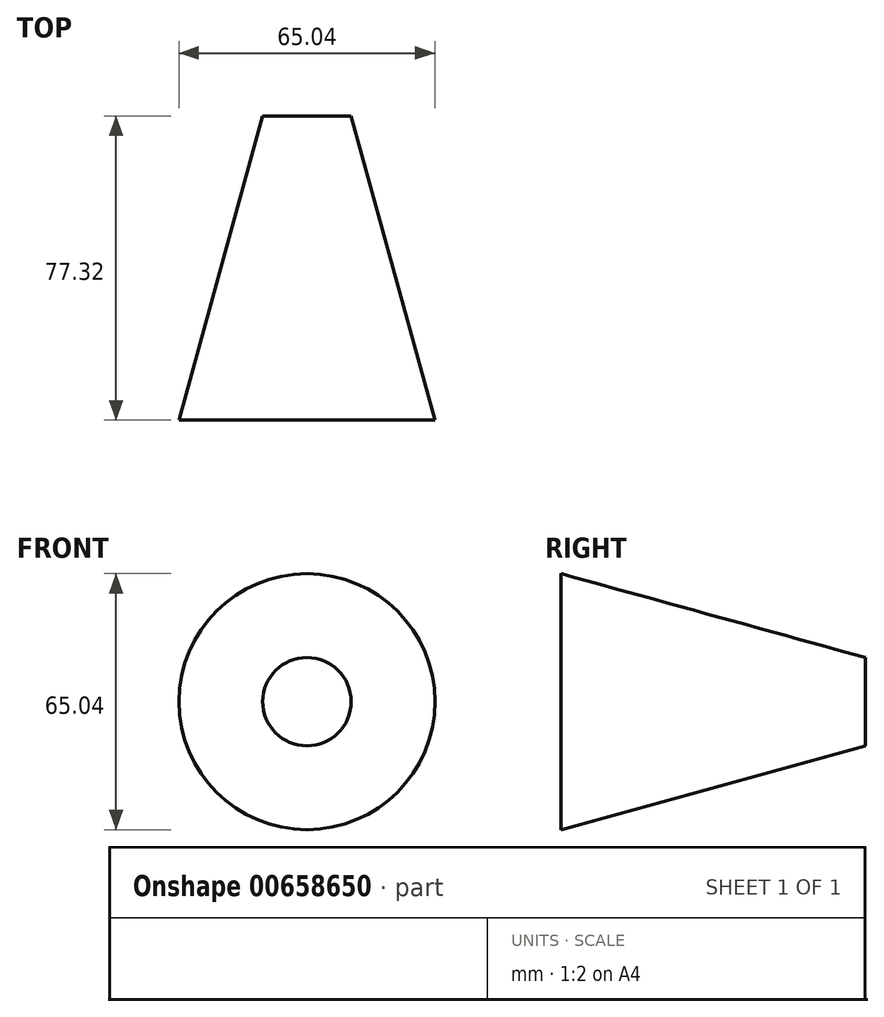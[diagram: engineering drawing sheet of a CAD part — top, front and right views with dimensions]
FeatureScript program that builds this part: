
annotation { "Feature Type Name" : "Feature", "Feature Type Description" : "" }
export const myFeature = defineFeature(function(context is Context, id is Id, definition is map)
    precondition{}
    {
        {
            var Q0;
            Q0=qCreatedBy(makeId("Top.planeOp"),FACE);
            var sketch = newSketch(context, id + "F0", { "sketchPlane" : qUnion([Q0])});
            skLineSegment(sketch, "E0", {"start": v(-11.23, 26.85) * mm, "end": v(-32.52, -50.47) * mm});
            skLineSegment(sketch, "E1", {"start": v(-32.52, -50.47) * mm, "end": v(0, -50.47) * mm});
            skLineSegment(sketch, "E2", {"start": v(0, -50.47) * mm, "end": v(0, 20.4) * mm});
            skSolve(sketch);
        }
        {
            var Q0;
            Q0=sQuery(id+"F0.wireOp",EDGE,"E0");
            var Q1;
            Q1=sQuery(id+"F0.wireOp",EDGE,"E2");
            revolve(context, id + "F1", {"bodyType" : ToolBodyType.SURFACE, "surfaceEntities" : qUnion([Q0]), "axis" : qUnion([Q1]), "revolveType" : RevolveType.FULL});
        }
    });
